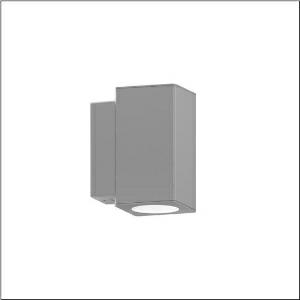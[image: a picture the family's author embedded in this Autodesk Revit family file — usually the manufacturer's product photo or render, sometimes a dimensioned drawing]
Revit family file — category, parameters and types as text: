
# Revit family: cl_31_wand_5cl553613
name_source: partatom
category: Lighting Fixtures
units: mm (PartAtom-declared; Revit-internal decimal feet)

## family parameters
Cut with Voids When Loaded = No
Host = Face
Light Source = No
Part Type = Normal
Room Calculation Point = No
Round Connector Dimension = Use Diameter
Shared = No

## types (1)
- --- (1 x LED, 300 lm, 2.8 W, 3000K)
    Apparent Load = 3 VA
    CIE Flux Codes = 98 100 100 100 100
    Color Rendering = 80
    Color Temperature = 3000K
    Default Elevation = 1800 mm
    Description = CL 31 Wall, wall luminaire, primary light control with reflector, of aluminium, primary optical cover: cover panel, of glass, transparent, light emission: down distribution, primary light characteristic: symmetric, installation type: surface-mounted, for 1x LED, rated luminous flux: 300lm, luminous efficacy: 106lm/W, light colour: 830, colour temperature: 3000K, control gear: DALI, with terminal, 5-pole, max. 2.5mm², mains connection: 220..240V, AC, 50/60Hz, rated input power: 2.8W, luminaire housing, square, of aluminium, powder-coated, Siteco® metallic grey, length: 143mm, width: 100mm, height: 186mm, protection rating (complete): IP65, insulation class (complete): insulation class I (protective earthing), certification: CE, ENEC, impact resistance: IK08, permissible operating ambient temperature for outdoor applications: -20..+50°C, packaging unit: 1 piece
    Height = 186 mm
    Lamp = 1 x LED
    Lamp Light Flux = 300 lm
    Lamp Power = 2.8 W
    Lamp count = 1
    Length = 100 mm  [stored 0.328084 ft]
    Luminous efficacy = 107 lm/W
    Manufacturer = Siteco
    ModVariant = No
    Model = 5CL553613
    Mounting Place = Wall
    Mounting Type = Surface mounted
    Number of Poles = 1
    OnlyDefault = Yes
    Power Factor = 1
    Product Name = CL 31 Wand
    Product group = wall luminaire
    ProductGroupID = 2002
    Protection Class = Protection class I
    Protection Degree = IP 65
    RLX_Detail_Level = 1
    RLX_Emergency_Light_Flux = 0 lm
    RLX_Emergency_Type = 0
    RLX_Emergency_Type_DB = No
    RlxData = <blob elided: 42689 chars, md5=c0c5e7e5>
    Socket = socket
    Standby Power = 0 W
    System Light Flux = 300 lm
    System Power = 3 W
    Type Comments = factory setting: luminous flux: 100 % | dim-lin: 254 | 70 mA
    Type Image = l_1006895.jpg
    URL = http://relux.com
    VarID = @adj_216815
    Voltage = 0 V
    Weight = 0.00 kg
    Width = 143 mm

note: [stored X ft] marks values corroborated as IEEE doubles in the binary element streams (Revit-internal decimal feet)

## geometry (parser evidence)
native form markers: Blend x4, Sweep x8
no freeform markers — native parametric forms only
